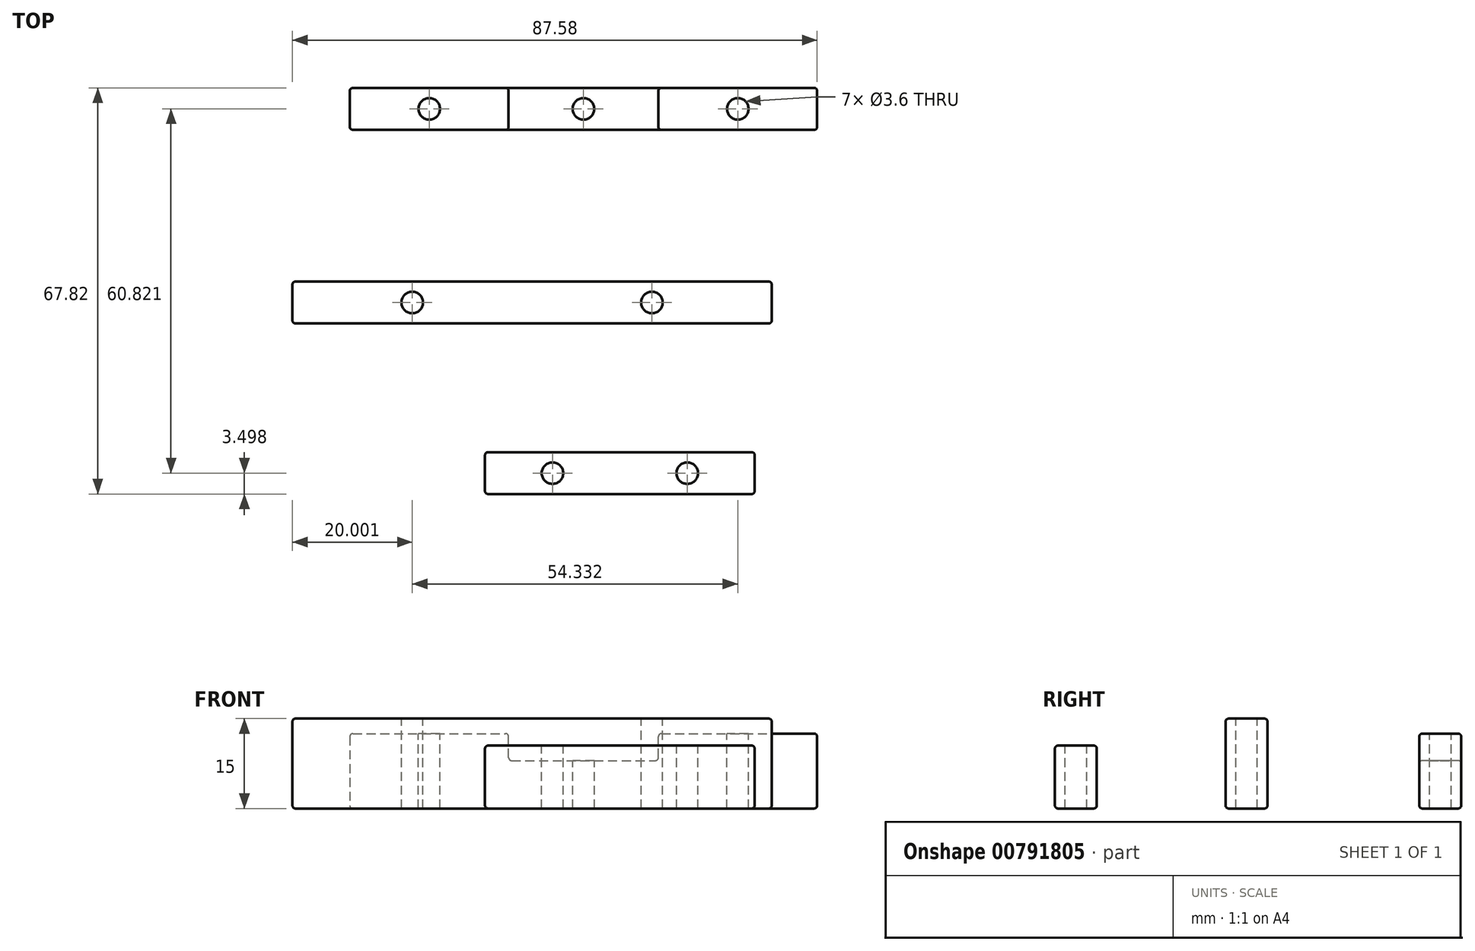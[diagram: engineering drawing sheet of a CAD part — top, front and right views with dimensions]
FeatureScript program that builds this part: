
annotation { "Feature Type Name" : "Feature", "Feature Type Description" : "" }
export const myFeature = defineFeature(function(context is Context, id is Id, definition is map)
    precondition{}
    {
        {
            var Q0;
            Q0=qCreatedBy(makeId("Top.planeOp"),FACE);
            var sketch = newSketch(context, id + "F0", { "sketchPlane" : qUnion([Q0])});
            skLineSegment(sketch, "E0.bottom", {"start": v(-27.73, 24.06) * mm, "end": v(50.27, 24.06) * mm});
            skLineSegment(sketch, "E0.top", {"start": v(-27.73, 17.06) * mm, "end": v(50.27, 17.06) * mm});
            skLineSegment(sketch, "E0.left", {"start": v(-27.73, 24.06) * mm, "end": v(-27.73, 17.06) * mm});
            skLineSegment(sketch, "E0.right", {"start": v(50.27, 24.06) * mm, "end": v(50.27, 17.06) * mm});
            skSolve(sketch);
        }
        {
            var Q0;
            Q0 = qSketchRegion(id + "F0", true);
            extrude(context, id + "F1", {"entities" : qUnion([Q0]), "depth" : 12.5 * mm, "offsetDistance" : 25 * mm});
        }
        {
            var Q0;
            Q0=makeQuery(id+"F1.opExtrude","CAP_FACE",FACE,{"disambiguationData":[OSD([sQuery(id+"F0.wireOp",EDGE,"E0.bottom"),sQuery(id+"F0.wireOp",EDGE,"E0.top"),sQuery(id+"F0.wireOp",EDGE,"E0.left"),sQuery(id+"F0.wireOp",EDGE,"E0.right")])],"isStart":false});
            var sketch = newSketch(context, id + "F2", { "sketchPlane" : qUnion([Q0])});
            skLineSegment(sketch, "E1.bottom", {"start": v(-1.23, 24.06) * mm, "end": v(23.77, 24.06) * mm});
            skLineSegment(sketch, "E1.top", {"start": v(-1.23, 17.06) * mm, "end": v(23.77, 17.06) * mm});
            skLineSegment(sketch, "E1.left", {"start": v(-1.23, 24.06) * mm, "end": v(-1.23, 17.06) * mm});
            skLineSegment(sketch, "E1.right", {"start": v(23.77, 24.06) * mm, "end": v(23.77, 17.06) * mm});
            skSolve(sketch);
        }
        {
            var Q0;
            Q0 = qSketchRegion(id + "F2", true);
            extrude(context, id + "F3", {"entities" : qUnion([Q0]), "operationType" : NewBodyOperationType.REMOVE, "oppositeDirection" : true, "depth" : 4.5 * mm, "offsetDistance" : 25 * mm});
        }
        {
            var Q0;
            {var subQ0=sQuery(id+"F0.wireOp",EDGE,"E0.bottom");var subQ1=sQuery(id+"F0.wireOp",EDGE,"E0.right");var subQ2=sQuery(id+"F0.wireOp",EDGE,"E0.top");Q0=makeQuery(id+"F3.boolean.opBoolean","SPLIT",FACE,{"disambiguationData":[TD([makeQuery(id+"F1.opExtrude","SWEPT_FACE",FACE,{"disambiguationData":[OSD([subQ1])]})])],"derivedFrom":makeQuery(id+"F1.opExtrude","CAP_FACE",FACE,{"disambiguationData":[OSD([subQ0,subQ2,sQuery(id+"F0.wireOp",EDGE,"E0.left"),subQ1])],"isStart":false})});}
            var Q1;
            {var subQ0=sQuery(id+"F0.wireOp",EDGE,"E0.bottom");var subQ1=sQuery(id+"F0.wireOp",EDGE,"E0.top");var subQ2=sQuery(id+"F0.wireOp",EDGE,"E0.left");Q1=makeQuery(id+"F3.boolean.opBoolean","SPLIT",FACE,{"disambiguationData":[TD([makeQuery(id+"F1.opExtrude","SWEPT_FACE",FACE,{"disambiguationData":[OSD([subQ2])]})])],"derivedFrom":makeQuery(id+"F1.opExtrude","CAP_FACE",FACE,{"disambiguationData":[OSD([subQ0,subQ1,subQ2,sQuery(id+"F0.wireOp",EDGE,"E0.right")])],"isStart":false})});}
            var Q2;
            Q2=makeQuery(id+"F3.boolean.opBoolean","COPY",FACE,{"derivedFrom":makeQuery(id+"F3.opExtrude","CAP_FACE",FACE,{"disambiguationData":[OSD([sQuery(id+"F2.wireOp",EDGE,"E1.bottom"),sQuery(id+"F2.wireOp",EDGE,"E1.top"),sQuery(id+"F2.wireOp",EDGE,"E1.left"),sQuery(id+"F2.wireOp",EDGE,"E1.right")])],"isStart":false})});
            var Q3;
            Q3=makeQuery(id+"F3.boolean.opBoolean","COPY",FACE,{"derivedFrom":makeQuery(id+"F3.opExtrude","SWEPT_FACE",FACE,{"disambiguationData":[OSD([sQuery(id+"F2.wireOp",EDGE,"E1.left")])]})});
            var Q4;
            Q4=makeQuery(id+"F3.boolean.opBoolean","COPY",FACE,{"derivedFrom":makeQuery(id+"F3.opExtrude","SWEPT_FACE",FACE,{"disambiguationData":[OSD([sQuery(id+"F2.wireOp",EDGE,"E1.right")])]})});
            var Q5;
            Q5=makeQuery(id+"F1.opExtrude","SWEPT_FACE",FACE,{"disambiguationData":[OSD([sQuery(id+"F0.wireOp",EDGE,"E0.right")])]});
            var Q6;
            Q6=makeQuery(id+"F1.opExtrude","SWEPT_FACE",FACE,{"disambiguationData":[OSD([sQuery(id+"F0.wireOp",EDGE,"E0.left")])]});
            var Q7;
            Q7=makeQuery(id+"F1.opExtrude","SWEPT_FACE",FACE,{"disambiguationData":[OSD([sQuery(id+"F0.wireOp",EDGE,"E0.top")])]});
            var Q8;
            Q8=makeQuery(id+"F1.opExtrude","SWEPT_FACE",FACE,{"disambiguationData":[OSD([sQuery(id+"F0.wireOp",EDGE,"E0.bottom")])]});
            fillet(context, id + "F4", {"entities" : qUnion([Q0, Q1, Q2, Q3, Q4, Q5, Q6, Q7, Q8]), "radius" : 0.5 * mm, "tangentPropagation" : true, "allowEdgeOverflow" : false});
        }
        {
            var Q0;
            {var subQ0=sQuery(id+"F0.wireOp",EDGE,"E0.bottom");var subQ1=sQuery(id+"F0.wireOp",EDGE,"E0.right");var subQ2=sQuery(id+"F0.wireOp",EDGE,"E0.top");Q0=makeQuery(id+"F3.boolean.opBoolean","SPLIT",FACE,{"disambiguationData":[TD([makeQuery(id+"F1.opExtrude","SWEPT_FACE",FACE,{"disambiguationData":[OSD([subQ1])]})])],"derivedFrom":makeQuery(id+"F1.opExtrude","CAP_FACE",FACE,{"disambiguationData":[OSD([subQ0,subQ2,sQuery(id+"F0.wireOp",EDGE,"E0.left"),subQ1])],"isStart":false})});}
            var sketch = newSketch(context, id + "F5", { "sketchPlane" : qUnion([Q0])});
            skCircle(sketch, "E2", {"center": v(37.02, 20.56) * mm, "radius": 1.8 * mm});
            skPoint(sketch, "E2.centerSnap0", {"position": v(37.02, 23.56) * mm});
            skPoint(sketch, "E2.centerSnap1", {"position": v(49.77, 20.56) * mm});
            skSolve(sketch);
        }
        {
            var Q0;
            Q0 = qSketchRegion(id + "F5", true);
            extrude(context, id + "F6", {"entities" : qUnion([Q0]), "operationType" : NewBodyOperationType.REMOVE, "oppositeDirection" : true, "depth" : 25 * mm, "offsetDistance" : 25 * mm});
        }
        {
            var Q0;
            {var subQ0=sQuery(id+"F0.wireOp",EDGE,"E0.bottom");var subQ1=sQuery(id+"F0.wireOp",EDGE,"E0.top");var subQ2=sQuery(id+"F0.wireOp",EDGE,"E0.left");Q0=makeQuery(id+"F3.boolean.opBoolean","SPLIT",FACE,{"disambiguationData":[TD([makeQuery(id+"F1.opExtrude","SWEPT_FACE",FACE,{"disambiguationData":[OSD([subQ2])]})])],"derivedFrom":makeQuery(id+"F1.opExtrude","CAP_FACE",FACE,{"disambiguationData":[OSD([subQ0,subQ1,subQ2,sQuery(id+"F0.wireOp",EDGE,"E0.right")])],"isStart":false})});}
            var sketch = newSketch(context, id + "F7", { "sketchPlane" : qUnion([Q0])});
            skCircle(sketch, "E3", {"center": v(-14.48, 20.56) * mm, "radius": 1.8 * mm});
            skPoint(sketch, "E3.centerSnap0", {"position": v(-14.48, 23.56) * mm});
            skPoint(sketch, "E3.centerSnap1", {"position": v(-27.23, 20.56) * mm});
            skSolve(sketch);
        }
        {
            var Q0;
            Q0 = qSketchRegion(id + "F7", true);
            extrude(context, id + "F8", {"entities" : qUnion([Q0]), "operationType" : NewBodyOperationType.REMOVE, "oppositeDirection" : true, "depth" : 25 * mm, "offsetDistance" : 25 * mm});
        }
        {
            var Q0;
            Q0=makeQuery(id+"F3.boolean.opBoolean","COPY",FACE,{"derivedFrom":makeQuery(id+"F3.opExtrude","CAP_FACE",FACE,{"disambiguationData":[OSD([sQuery(id+"F2.wireOp",EDGE,"E1.bottom"),sQuery(id+"F2.wireOp",EDGE,"E1.top"),sQuery(id+"F2.wireOp",EDGE,"E1.left"),sQuery(id+"F2.wireOp",EDGE,"E1.right")])],"isStart":false})});
            var sketch = newSketch(context, id + "F9", { "sketchPlane" : qUnion([Q0])});
            skCircle(sketch, "E4", {"center": v(11.27, 20.56) * mm, "radius": 1.8 * mm});
            skPoint(sketch, "E4.centerSnap0", {"position": v(-0.73, 20.56) * mm});
            skPoint(sketch, "E4.centerSnap1", {"position": v(11.27, 23.56) * mm});
            skSolve(sketch);
        }
        {
            var Q0;
            Q0 = qSketchRegion(id + "F9", true);
            extrude(context, id + "F10", {"entities" : qUnion([Q0]), "operationType" : NewBodyOperationType.REMOVE, "oppositeDirection" : true, "depth" : 25 * mm, "offsetDistance" : 25 * mm});
        }
        {
            var Q0;
            Q0=qCreatedBy(makeId("Top.planeOp"),FACE);
            var sketch = newSketch(context, id + "F11", { "sketchPlane" : qUnion([Q0])});
            skLineSegment(sketch, "E5.bottom", {"start": v(-83.5, -8.28) * mm, "end": v(-3.5, -8.28) * mm});
            skLineSegment(sketch, "E5.top", {"start": v(-83.5, -15.28) * mm, "end": v(-3.5, -15.28) * mm});
            skLineSegment(sketch, "E5.left", {"start": v(-83.5, -8.28) * mm, "end": v(-83.5, -15.28) * mm});
            skLineSegment(sketch, "E5.right", {"start": v(-3.5, -8.28) * mm, "end": v(-3.5, -15.28) * mm});
            skSolve(sketch);
        }
        {
            var Q0;
            Q0 = qSketchRegion(id + "F11", true);
            extrude(context, id + "F12", {"entities" : qUnion([Q0]), "depth" : 15 * mm, "offsetDistance" : 25 * mm});
        }
        {
            var Q0;
            Q0=makeQuery(id+"F12.opExtrude","CAP_FACE",FACE,{"disambiguationData":[OSD([sQuery(id+"F11.wireOp",EDGE,"E5.bottom"),sQuery(id+"F11.wireOp",EDGE,"E5.top"),sQuery(id+"F11.wireOp",EDGE,"E5.left"),sQuery(id+"F11.wireOp",EDGE,"E5.right")])],"isStart":false});
            var sketch = newSketch(context, id + "F13", { "sketchPlane" : qUnion([Q0])});
            skCircle(sketch, "E6", {"center": v(-63.5, -11.78) * mm, "radius": 1.8 * mm});
            skPoint(sketch, "E6.centerSnap0", {"position": v(-83.5, -11.78) * mm});
            skCircle(sketch, "E7", {"center": v(-23.5, -11.78) * mm, "radius": 1.8 * mm});
            skPoint(sketch, "E7.centerSnap0", {"position": v(-3.5, -11.78) * mm});
            skSolve(sketch);
        }
        {
            var Q0;
            Q0 = qSketchRegion(id + "F13", true);
            extrude(context, id + "F14", {"entities" : qUnion([Q0]), "operationType" : NewBodyOperationType.REMOVE, "oppositeDirection" : true, "depth" : 25 * mm, "offsetDistance" : 25 * mm});
        }
        {
            var Q0;
            Q0=makeQuery(id+"F12.opExtrude","SWEPT_FACE",FACE,{"disambiguationData":[OSD([sQuery(id+"F11.wireOp",EDGE,"E5.top")])]});
            var Q1;
            Q1=makeQuery(id+"F12.opExtrude","SWEPT_FACE",FACE,{"disambiguationData":[OSD([sQuery(id+"F11.wireOp",EDGE,"E5.left")])]});
            var Q2;
            Q2=makeQuery(id+"F12.opExtrude","SWEPT_FACE",FACE,{"disambiguationData":[OSD([sQuery(id+"F11.wireOp",EDGE,"E5.bottom")])]});
            var Q3;
            Q3=makeQuery(id+"F12.opExtrude","SWEPT_FACE",FACE,{"disambiguationData":[OSD([sQuery(id+"F11.wireOp",EDGE,"E5.right")])]});
            fillet(context, id + "F15", {"entities" : qUnion([Q0, Q1, Q2, Q3]), "radius" : 0.5 * mm, "tangentPropagation" : true, "allowEdgeOverflow" : false});
        }
        {
            var Q0;
            Q0=makeQuery(id+"F12.opExtrude","SWEPT_BODY",BODY,{"disambiguationData":[OSD([sQuery(id+"F11.wireOp",EDGE,"E5.bottom"),sQuery(id+"F11.wireOp",EDGE,"E5.top"),sQuery(id+"F11.wireOp",EDGE,"E5.left"),sQuery(id+"F11.wireOp",EDGE,"E5.right")])]});
            transform(context, id + "F16", {"entities" : qUnion([Q0]), "transformType" : TransformType.TRANSLATION_3D, "dx" : 46.2 * mm, "dy" : 0 * mm, "dz" : 0 * mm, "makeCopy" : false});
        }
        {
            var Q0;
            Q0=qCreatedBy(makeId("Top.planeOp"),FACE);
            var sketch = newSketch(context, id + "F17", { "sketchPlane" : qUnion([Q0])});
            skLineSegment(sketch, "E8.bottom", {"start": v(-5.16, -36.76) * mm, "end": v(39.84, -36.76) * mm});
            skLineSegment(sketch, "E8.top", {"start": v(-5.16, -43.76) * mm, "end": v(39.84, -43.76) * mm});
            skLineSegment(sketch, "E8.left", {"start": v(-5.16, -36.76) * mm, "end": v(-5.16, -43.76) * mm});
            skLineSegment(sketch, "E8.right", {"start": v(39.84, -36.76) * mm, "end": v(39.84, -43.76) * mm});
            skSolve(sketch);
        }
        {
            var Q0;
            Q0 = qSketchRegion(id + "F17", true);
            extrude(context, id + "F18", {"entities" : qUnion([Q0]), "depth" : 10.5 * mm, "offsetDistance" : 25 * mm});
        }
        {
            var Q0;
            Q0=makeQuery(id+"F18.opExtrude","CAP_FACE",FACE,{"disambiguationData":[OSD([sQuery(id+"F17.wireOp",EDGE,"E8.bottom"),sQuery(id+"F17.wireOp",EDGE,"E8.top"),sQuery(id+"F17.wireOp",EDGE,"E8.left"),sQuery(id+"F17.wireOp",EDGE,"E8.right")])],"isStart":false});
            var sketch = newSketch(context, id + "F19", { "sketchPlane" : qUnion([Q0])});
            skCircle(sketch, "E9", {"center": v(6.09, -40.26) * mm, "radius": 1.8 * mm});
            skPoint(sketch, "E9.centerSnap0", {"position": v(-5.16, -40.26) * mm});
            skCircle(sketch, "E10", {"center": v(28.59, -40.26) * mm, "radius": 1.8 * mm});
            skPoint(sketch, "E10.centerSnap0", {"position": v(39.84, -40.26) * mm});
            skSolve(sketch);
        }
        {
            var Q0;
            Q0 = qSketchRegion(id + "F19", true);
            extrude(context, id + "F20", {"entities" : qUnion([Q0]), "operationType" : NewBodyOperationType.REMOVE, "oppositeDirection" : true, "depth" : 25 * mm, "offsetDistance" : 25 * mm});
        }
        {
            var Q0;
            Q0=makeQuery(id+"F18.opExtrude","SWEPT_FACE",FACE,{"disambiguationData":[OSD([sQuery(id+"F17.wireOp",EDGE,"E8.top")])]});
            var Q1;
            Q1=makeQuery(id+"F18.opExtrude","SWEPT_FACE",FACE,{"disambiguationData":[OSD([sQuery(id+"F17.wireOp",EDGE,"E8.right")])]});
            var Q2;
            Q2=makeQuery(id+"F18.opExtrude","SWEPT_FACE",FACE,{"disambiguationData":[OSD([sQuery(id+"F17.wireOp",EDGE,"E8.left")])]});
            var Q3;
            Q3=makeQuery(id+"F18.opExtrude","SWEPT_FACE",FACE,{"disambiguationData":[OSD([sQuery(id+"F17.wireOp",EDGE,"E8.bottom")])]});
            fillet(context, id + "F21", {"entities" : qUnion([Q0, Q1, Q2, Q3]), "radius" : 0.5 * mm, "tangentPropagation" : true, "allowEdgeOverflow" : false});
        }
    });
